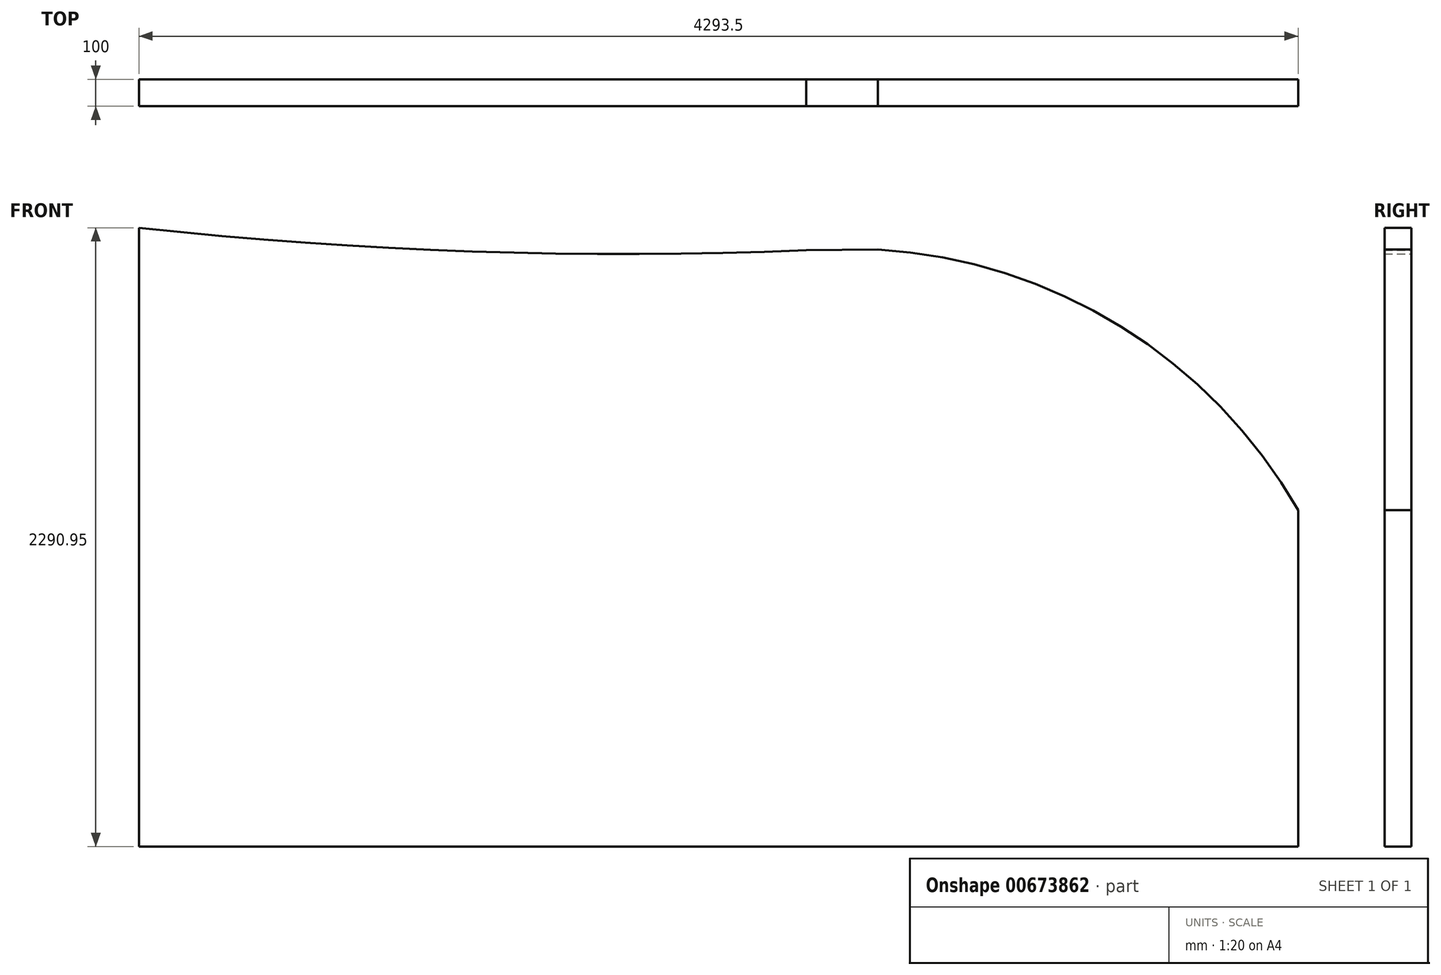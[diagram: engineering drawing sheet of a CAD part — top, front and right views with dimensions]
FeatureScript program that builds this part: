
annotation { "Feature Type Name" : "Feature", "Feature Type Description" : "" }
export const myFeature = defineFeature(function(context is Context, id is Id, definition is map)
    precondition{}
    {
        {
            var Q0;
            Q0=qCreatedBy(makeId("Front.planeOp"),FACE);
            var sketch = newSketch(context, id + "F0", { "sketchPlane" : qUnion([Q0])});
            skArc(sketch, "E0", {"start": v(2087.17, -48.65) * mm, "mid": v(1430.99, 631.3) * mm, "end": v(530.27, 917) * mm});
            skArc(sketch, "E1", {"start": v(-2206.33, 997.48) * mm, "mid": v(-972.04, 909.7) * mm, "end": v(265.36, 914.07) * mm});
            skLineSegment(sketch, "E2", {"start": v(2087.17, -48.65) * mm, "end": v(2087.17, -1293.47) * mm});
            skLineSegment(sketch, "E3", {"start": v(265.36, 914.07) * mm, "end": v(530.27, 917) * mm});
            skLineSegment(sketch, "E4", {"start": v(2087.17, -1293.47) * mm, "end": v(-2206.33, -1293.47) * mm});
            skLineSegment(sketch, "E5", {"start": v(-2206.33, -1293.47) * mm, "end": v(-2206.33, 997.48) * mm});
            skSolve(sketch);
        }
        {
            var Q0;
            Q0 = qSketchRegion(id + "F0", true);
            extrude(context, id + "F1", {"entities" : qUnion([Q0]), "depth" : 100 * mm, "offsetDistance" : 25 * mm});
        }
    });
